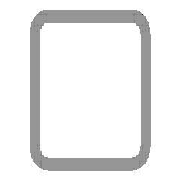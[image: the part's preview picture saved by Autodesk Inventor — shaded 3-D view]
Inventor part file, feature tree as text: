
AUTODESK INVENTOR PART (.ipt)
format: ipt  version: 2025.1 (Build 291241020, 241B)  size: 144,384 bytes
history: native  units: mm (DEFAULTED — no unit token found)
features: other x4, sketch x1, plane x1
ambient origin geometry x8: Origin, YZ Plane, XZ Plane, XY Plane, X Axis, Y Axis, Z Axis, Center Point
bodies: Solid1 (feature_tree), Body (feature_tree)
feature tree (6):
  parser-record x1  (decoder bookkeeping rows leaked as tree rows — omitted from the tree; the rows remain in map.json)
  other  "Driven Length"
  other  "Start plane"
  other  "End plane"
  sketch  "Sketch3"  dims[d3=550.0mm d4=0.0mm d7=6.0mm d9=100.0mm d11=100.0mm d12=3.0mm d13=100.0mm d14=650.0mm d15=50.0mm d16=50.0mm d17=90.0deg d18=550.0mm]
  plane  "Work Plane3"
